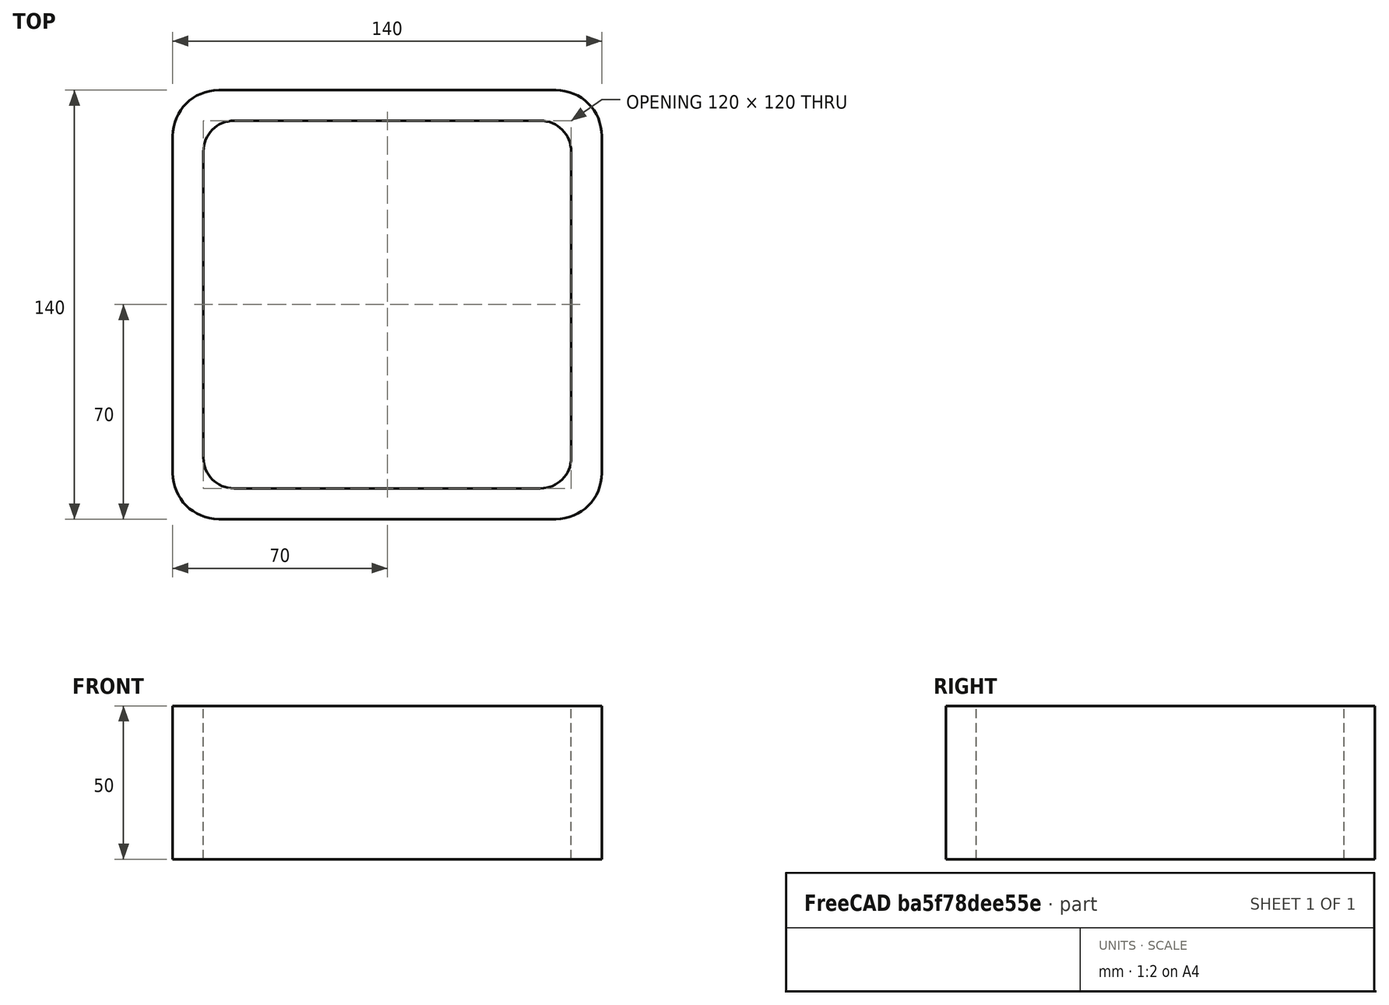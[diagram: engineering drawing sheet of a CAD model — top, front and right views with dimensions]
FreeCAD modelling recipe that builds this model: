
FCSTD DOCUMENT  (FreeCAD 0.15R4671 (Git))
Label: Square hollow section 140x140x10 EN10219 S235JRH
License: All rights reserved
LicenseURL: http://en.wikipedia.org/wiki/All_rights_reserved
objects: Sketcher::SketchObject×1, Part::Extrusion×1
note: 2 computed .brp shape members not serialized (recipe doc carries the construction recipe); baked Part::Feature solids carry a one-line shape summary decoded from their .brp

FEATURE [Sketcher::SketchObject] Sketch
  sketch-geometry (16):
    g0: LineSegment StartX=-50 StartY=60 StartZ=0 EndX=50 EndY=60 EndZ=0
    g1: LineSegment StartX=60 StartY=50 StartZ=0 EndX=60 EndY=-50 EndZ=0
    g2: LineSegment StartX=50 StartY=-60 StartZ=0 EndX=-50 EndY=-60 EndZ=0
    g3: LineSegment StartX=-60 StartY=-50 StartZ=0 EndX=-60 EndY=50 EndZ=0
    g4: LineSegment StartX=-55 StartY=70 StartZ=0 EndX=55 EndY=70 EndZ=0
    g5: LineSegment StartX=70 StartY=55 StartZ=0 EndX=70 EndY=-55 EndZ=0
    g6: LineSegment StartX=55 StartY=-70 StartZ=0 EndX=-55 EndY=-70 EndZ=0
    g7: LineSegment StartX=-70 StartY=-55 StartZ=0 EndX=-70 EndY=55 EndZ=0
    g8: ArcOfCircle CenterX=-50 CenterY=50 CenterZ=0 NormalX=0 NormalY=0 NormalZ=1 Radius=10 StartAngle=1.5708 EndAngle=3.14159
    g9: ArcOfCircle CenterX=50 CenterY=50 CenterZ=0 NormalX=0 NormalY=0 NormalZ=1 Radius=10 StartAngle=0 EndAngle=1.5708
    g10: ArcOfCircle CenterX=50 CenterY=-50 CenterZ=0 NormalX=0 NormalY=0 NormalZ=1 Radius=10 StartAngle=4.71239 EndAngle=6.28319
    g11: ArcOfCircle CenterX=-50 CenterY=-50 CenterZ=0 NormalX=0 NormalY=0 NormalZ=1 Radius=10 StartAngle=3.14159 EndAngle=4.71239
    g12: ArcOfCircle CenterX=55 CenterY=55 CenterZ=0 NormalX=0 NormalY=0 NormalZ=1 Radius=15 StartAngle=0 EndAngle=1.5708
    g13: ArcOfCircle CenterX=55 CenterY=-55 CenterZ=0 NormalX=0 NormalY=0 NormalZ=1 Radius=15 StartAngle=4.71239 EndAngle=6.28319
    g14: ArcOfCircle CenterX=-55 CenterY=-55 CenterZ=0 NormalX=0 NormalY=0 NormalZ=1 Radius=15 StartAngle=3.14159 EndAngle=4.71239
    g15: ArcOfCircle CenterX=-55 CenterY=55 CenterZ=0 NormalX=0 NormalY=0 NormalZ=1 Radius=15 StartAngle=1.5708 EndAngle=3.14159
  constraints (36):
    c: Horizontal(g2)
    c: Vertical(g3)
    c: Horizontal(g6)
    c: Vertical(g7)
    c: Tangent(g3,g8) = 1.5708
    c: Tangent(g0,g8) = 1.5708
    c: Tangent(g0,g9) = 1.5708
    c: Tangent(g1,g9) = 1.5708
    c: Tangent(g1,g10) = 1.5708
    c: Tangent(g2,g10) = 1.5708
    c: Tangent(g2,g11) = 1.5708
    c: Tangent(g3,g11) = 1.5708
    c: Tangent(g4,g12) = 1.5708
    c: Tangent(g5,g12) = 1.5708
    c: Tangent(g5,g13) = 1.5708
    c: Tangent(g6,g13) = 1.5708
    c: Tangent(g6,g14) = 1.5708
    c: Tangent(g7,g14) = 1.5708
    c: Tangent(g7,g15) = 1.5708
    c: Tangent(g4,g15) = 1.5708
    c: Equal(g9,g8)
    c: Equal(g9,g11)
    c: Equal(g9,g10)
    c: Equal(g12,g15)
    c: Equal(g12,g14)
    c: Equal(g12,g13)
    c: Symmetric(g4,g6,g-1)
    c: Symmetric(g7,g5,g-2)
    c: DistanceY(g4,g6) = -140
    c: DistanceX(g7,g5) = 140
    c: Symmetric(g3,g1,g-2)
    c: Symmetric(g0,g2,g-1)
    c: DistanceY(g0,g4) = 10
    c: DistanceX(g5,g1) = -10
    c: Radius(g9) = 10
    c: Radius(g12) = 15
FEATURE [Part::Extrusion] Extrude  label="Square hollow section 140x140x10 EN10219 S235JRH"
  Base = -> Sketch
  Dir = (0,0,50)
  Solid = true
